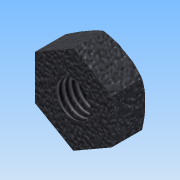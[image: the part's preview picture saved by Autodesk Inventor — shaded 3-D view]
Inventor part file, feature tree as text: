
AUTODESK INVENTOR PART (.ipt)
format: ipt  version: 2015 (Build 190159000, 159)  size: 123,904 bytes
history: native  units: mm
features: sketch x4, extrude x1, revolve x1, hole x1, projected_geometry x1
ambient origin geometry x8: Origin, YZ Plane, XZ Plane, XY Plane, X Axis, Y Axis, Z Axis, Center Point
bodies: Solid1 (feature_tree)
feature tree (8):
  extrude  "Extrusion1"  Depth=6.5mm TaperAngle=0.0deg
  sketch  "Sketch2"  dims[d6=1.0mm d7=30.0deg]
  revolve  "Revolution1"  Angle=30.0deg
  hole  "Hole1"  [1 undecoded]
  sketch  "Sketch1"  dims[d0=15.0mm d1=6.5mm d2=0.0mm]
  sketch  "Sketch6"  dims[d8=90.0deg]
  projected_geometry  "Projected Loop2"
  sketch  "Sketch7"  dims[d9=6.647mm d10=6.0mm d11=4.0mm d12=2.0mm d13=90.0deg d14=12.75mm d15=20.594885mm]
note: 1 required parameter value undecoded (feature->parameter linkage not recoverable at this tier; creation-order binding heuristic only, values carry confidence <= 0.55)
